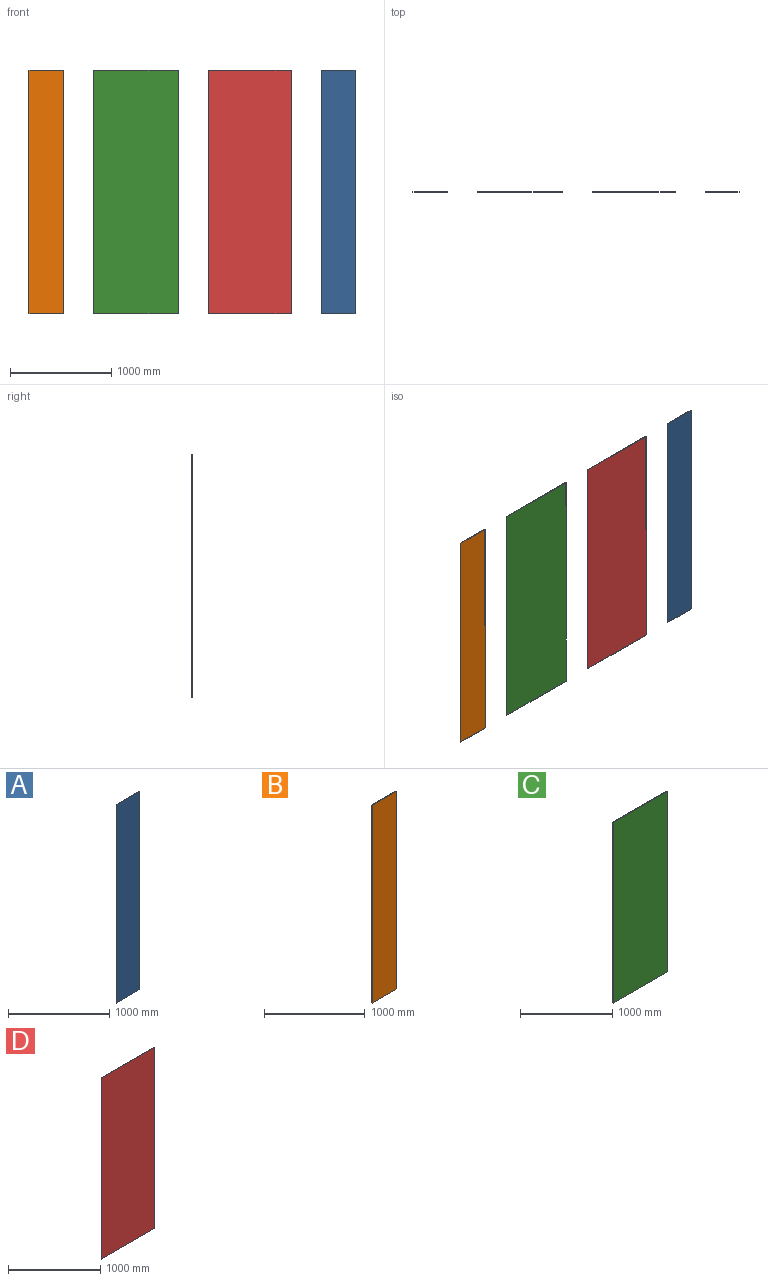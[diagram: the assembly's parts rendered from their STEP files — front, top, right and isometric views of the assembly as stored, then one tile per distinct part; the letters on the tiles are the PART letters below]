
ASSEMBLY  parts=4 mates=3
PART A: 6 faces, bbox 330x5x2400 mm
  f0: plane 330x5mm, normal (0,0,1), area 1650mm2, adj f1,f3,f4,f5
  f1: plane 2400x5mm, normal (-1,0,0), area 12000mm2, adj f0,f2,f4,f5
  f2: plane 330x5mm, normal (0,0,-1), area 1650mm2, adj f1,f3,f4,f5
  f3: plane 2400x5mm, normal (1,0,0), area 12000mm2, adj f0,f2,f4,f5
  f4: plane 2400x330mm, normal (0,-1,0), area 792000mm2, adj f0,f1,f2,f3
  f5: plane 2400x330mm, normal (0,1,0), area 792000mm2, adj f0,f1,f2,f3
PART B: 6 faces, bbox 340x5x2400 mm
  f0: plane 340x5mm, normal (0,0,-1), area 1700mm2, adj f1,f3,f4,f5
  f1: plane 2400x5mm, normal (1,0,0), area 12000mm2, adj f0,f2,f4,f5
  f2: plane 340x5mm, normal (0,0,1), area 1700mm2, adj f1,f3,f4,f5
  f3: plane 2400x5mm, normal (-1,0,0), area 12000mm2, adj f0,f2,f4,f5
  f4: plane 2400x340mm, normal (0,-1,0), area 816000mm2, adj f0,f1,f2,f3
  f5: plane 2400x340mm, normal (0,1,0), area 816000mm2, adj f0,f1,f2,f3
PART C: 6 faces, bbox 830x5x2400 mm
  f0: plane 830x5mm, normal (0,0,1), area 4150mm2, adj f1,f3,f4,f5
  f1: plane 2400x5mm, normal (-1,0,0), area 12000mm2, adj f0,f2,f4,f5
  f2: plane 830x5mm, normal (0,0,-1), area 4150mm2, adj f1,f3,f4,f5
  f3: plane 2400x5mm, normal (1,0,0), area 12000mm2, adj f0,f2,f4,f5
  f4: plane 2400x830mm, normal (0,-1,0), area 1992000mm2, adj f0,f1,f2,f3
  f5: plane 2400x830mm, normal (0,1,0), area 1992000mm2, adj f0,f1,f2,f3
PART D: 6 faces, bbox 815x5x2400 mm
  f0: plane 2400x5mm, normal (-1,0,0), area 12000mm2, adj f1,f3,f4,f5
  f1: plane 815x5mm, normal (0,0,-1), area 4075mm2, adj f0,f2,f4,f5
  f2: plane 2400x5mm, normal (1,0,0), area 12000mm2, adj f1,f3,f4,f5
  f3: plane 815x5mm, normal (0,0,1), area 4075mm2, adj f0,f2,f4,f5
  f4: plane 2400x815mm, normal (0,-1,0), area 1956000mm2, adj f0,f1,f2,f3
  f5: plane 2400x815mm, normal (0,1,0), area 1956000mm2, adj f0,f1,f2,f3
PLACE A t=(590,0,0)mm
PLACE B t=(-295,0,0)mm
PLACE C at identity
PLACE D t=(295,0,0)mm
MATE fastened D.f4 <-> C.f4  axis (0,-1,0) through (1475,-265,110)mm
MATE fastened D.f4 <-> A.f4  axis (0,-1,0) through (2290,-265,110)mm
MATE fastened B.f4 <-> C.f4  axis (0,-1,0) through (45,-265,110)mm
